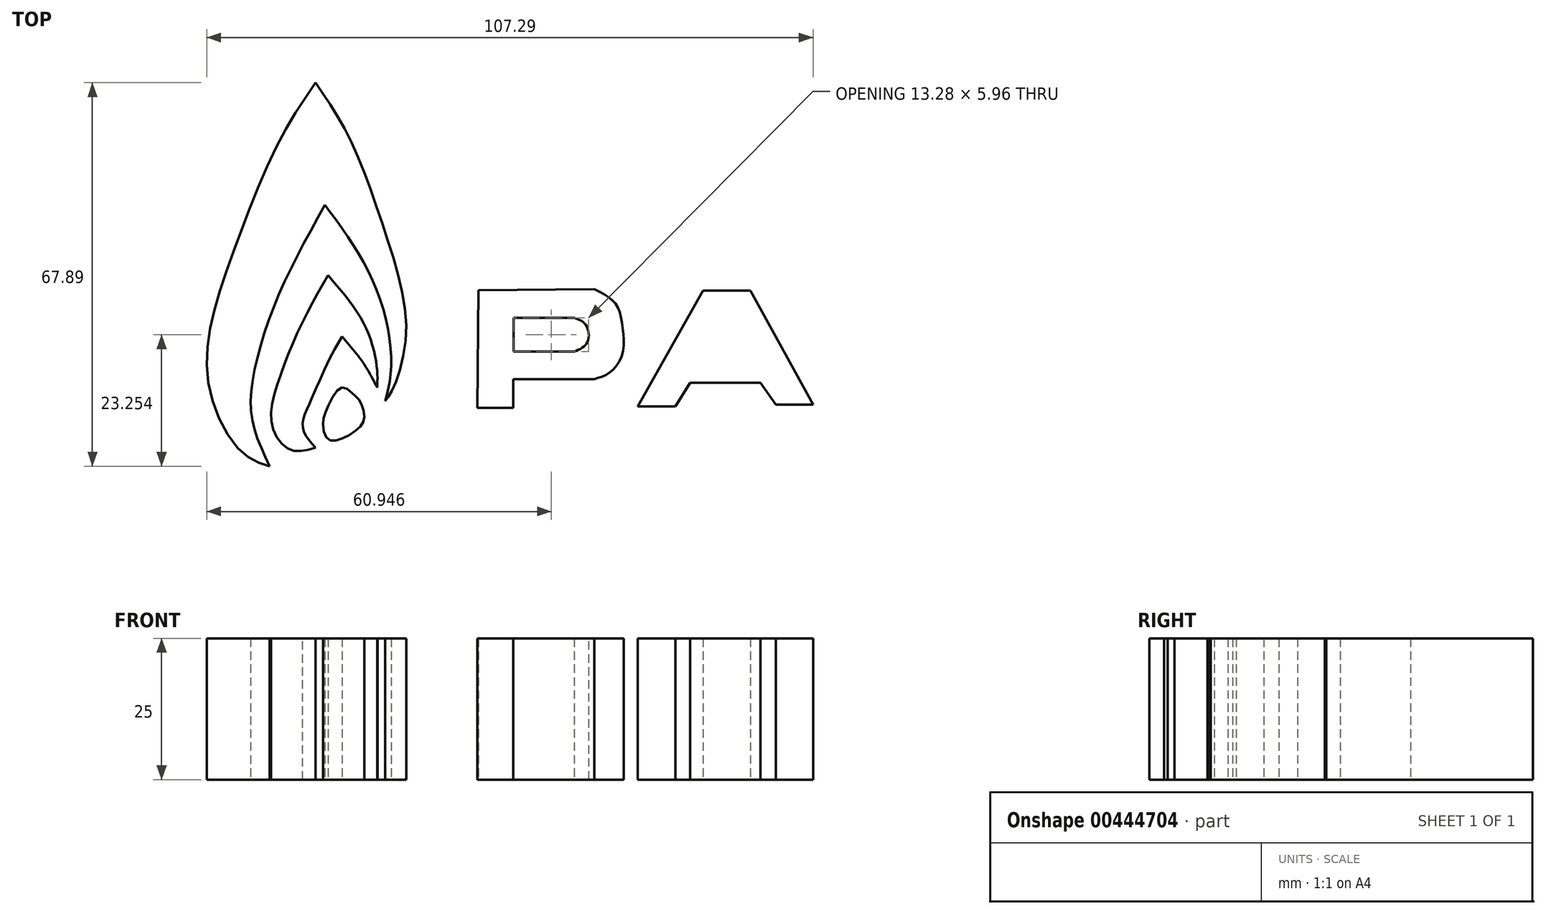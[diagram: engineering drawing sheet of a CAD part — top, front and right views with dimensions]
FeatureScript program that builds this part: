
annotation { "Feature Type Name" : "Feature", "Feature Type Description" : "" }
export const myFeature = defineFeature(function(context is Context, id is Id, definition is map)
    precondition{}
    {
        {
            var Q0;
            Q0=qCreatedBy(makeId("Top.planeOp"),FACE);
            var sketch = newSketch(context, id + "F0", { "sketchPlane" : qUnion([Q0])});
            skFitSpline(sketch, "E0", {"points": [v(-54.3, 49.44) * mm, v(-61.15, 38.22) * mm, v(-68.44, 20.5) * mm, v(-72.93, 5.9) * mm, v(-72.7, -6.22) * mm, v(-67.2, -16.09) * mm, v(-62.38, -18.45) * mm], "startDerivative": vector(-40.51, -59.93) * mm, "endDerivative": vector(44.37, -13.1) * mm});
            skFitSpline(sketch, "E1", {"points": [v(-62.38, -18.45) * mm, v(-65.4, -10.6) * mm, v(-65.19, -1.95) * mm, v(-60.8, 11.85) * mm, v(-52.62, 27.78) * mm], "startDerivative": vector(-17.84, 37.29) * mm, "endDerivative": vector(29.02, 52.05) * mm});
            skFitSpline(sketch, "E2", {"points": [v(-52.62, 27.78) * mm, v(-46.45, 18.8) * mm, v(-41.96, 8.15) * mm, v(-40.95, -1.61) * mm, v(-41.96, -6.89) * mm], "startDerivative": vector(23.8, -31.92) * mm, "endDerivative": vector(-6.8, -25.4) * mm});
            skFitSpline(sketch, "E3", {"points": [v(-41.96, -6.89) * mm, v(-40.72, -5) * mm, v(-38.25, 5.47) * mm, v(-41.96, 22.95) * mm, v(-48.32, 39.75) * mm, v(-54.3, 49.44) * mm], "startDerivative": vector(12.94, 16) * mm, "endDerivative": vector(-30.39, 43.69) * mm});
            skFitSpline(sketch, "E4", {"points": [v(-54.3, -15.17) * mm, v(-58.7, -15.57) * mm, v(-61.95, -11.32) * mm, v(-61.06, -4.1) * mm, v(-57.01, 6.16) * mm, v(-52.07, 15.35) * mm], "startDerivative": vector(-29.62, -8.98) * mm, "endDerivative": vector(21.55, 37.6) * mm});
            skFitSpline(sketch, "E5", {"points": [v(-52.07, 15.35) * mm, v(-45.46, 6.26) * mm, v(-43.38, -1.44) * mm, v(-43.38, -4.5) * mm], "startDerivative": vector(18, -20.75) * mm, "endDerivative": vector(-0.74, -12.27) * mm});
            skFitSpline(sketch, "E6", {"points": [v(-43.38, -4.5) * mm, v(-45.95, 0) * mm, v(-49.6, 4.48) * mm], "startDerivative": vector(-4.83, 9.4) * mm, "endDerivative": vector(-7.59, 8.6) * mm});
            skFitSpline(sketch, "E7", {"points": [v(-49.6, 4.48) * mm, v(-52.07, 0) * mm, v(-55.14, -6.89) * mm, v(-56.52, -11.62) * mm, v(-54.3, -15.17) * mm], "startDerivative": vector(-10.04, -17) * mm, "endDerivative": vector(13.81, -15.48) * mm});
            skFitSpline(sketch, "E8", {"points": [v(-49.6, -4.5) * mm, v(-52.07, -7.86) * mm, v(-52.96, -11.02) * mm, v(-52.07, -13.7) * mm, v(-49.6, -13.6) * mm, v(-46.45, -11.52) * mm, v(-45.65, -9.64) * mm, v(-46.45, -6.89) * mm, v(-47.63, -5.69) * mm, v(-49.6, -4.5) * mm]});
            skFitSpline(sketch, "E9", {"points": [v(-25.44, 12.72) * mm, v(-25.63, -8.14) * mm], "startDerivative": vector(-0.19, -20.86) * mm, "endDerivative": vector(-0.19, -20.86) * mm});
            skFitSpline(sketch, "E10", {"points": [v(-25.63, -8.14) * mm, v(-19.3, -8.14) * mm], "startDerivative": vector(6.33, 0) * mm, "endDerivative": vector(6.33, 0) * mm});
            skFitSpline(sketch, "E11", {"points": [v(-19.3, -8.14) * mm, v(-19.3, -3.02) * mm], "startDerivative": vector(0, 5.12) * mm, "endDerivative": vector(0, 5.12) * mm});
            skFitSpline(sketch, "E12", {"points": [v(-19.3, -3.02) * mm, v(-4.95, -3.02) * mm], "startDerivative": vector(14.34, 0) * mm, "endDerivative": vector(14.34, 0) * mm});
            skFitSpline(sketch, "E13", {"points": [v(-4.95, -3.02) * mm, v(-2.25, -1.9) * mm, v(0, 1.36) * mm, v(0, 6.67) * mm, v(-1.32, 10.49) * mm, v(-4.95, 12.9) * mm], "startDerivative": vector(16.44, 4.6) * mm, "endDerivative": vector(-20.28, 10.04) * mm});
            skFitSpline(sketch, "E14", {"points": [v(-25.44, 12.72) * mm, v(-4.95, 12.9) * mm], "startDerivative": vector(20.5, 0.19) * mm, "endDerivative": vector(20.5, 0.19) * mm});
            skLineSegment(sketch, "E15", {"start": v(-19.2, 7.32) * mm, "end": v(-19.2, 1.82) * mm});
            skLineSegment(sketch, "E16", {"start": v(-19.2, 1.82) * mm, "end": v(-8.5, 1.82) * mm});
            skFitSpline(sketch, "E17", {"points": [v(-8.5, 1.82) * mm, v(-6.16, 3.5) * mm, v(-6.44, 6.57) * mm, v(-8.5, 7.78) * mm], "startDerivative": vector(8.47, 3.6) * mm, "endDerivative": vector(-7.6, 2.47) * mm});
            skFitSpline(sketch, "E18", {"points": [v(-8.5, 7.78) * mm, v(-19.2, 7.78) * mm], "startDerivative": vector(-10.71, 0) * mm, "endDerivative": vector(-10.71, 0) * mm});
            skFitSpline(sketch, "E19", {"points": [v(-19.2, 7.78) * mm, v(-19.2, 7.32) * mm], "startDerivative": vector(0, -0.47) * mm, "endDerivative": vector(0, -0.47) * mm});
            skLineSegment(sketch, "E20", {"start": v(2.78, -7.86) * mm, "end": v(9.4, -7.86) * mm});
            skFitSpline(sketch, "E21", {"points": [v(9.4, -7.86) * mm, v(12, -3.67) * mm], "startDerivative": vector(2.6, 4.2) * mm, "endDerivative": vector(2.6, 4.2) * mm});
            skFitSpline(sketch, "E22", {"points": [v(12, -3.67) * mm, v(24.48, -3.67) * mm], "startDerivative": vector(12.48, 0) * mm, "endDerivative": vector(12.48, 0) * mm});
            skFitSpline(sketch, "E23", {"points": [v(24.48, -3.67) * mm, v(27.18, -7.58) * mm], "startDerivative": vector(2.7, -3.91) * mm, "endDerivative": vector(2.7, -3.91) * mm});
            skFitSpline(sketch, "E24", {"points": [v(27.18, -7.58) * mm, v(33.8, -7.58) * mm], "startDerivative": vector(6.61, 0) * mm, "endDerivative": vector(6.61, 0) * mm});
            skFitSpline(sketch, "E25", {"points": [v(33.89, -7.77) * mm, v(22.7, 12.63) * mm], "startDerivative": vector(-11.18, 20.4) * mm, "endDerivative": vector(-11.18, 20.4) * mm});
            skFitSpline(sketch, "E26", {"points": [v(22.7, 12.63) * mm, v(14.33, 12.63) * mm], "startDerivative": vector(-8.38, 0) * mm, "endDerivative": vector(-8.38, 0) * mm});
            skFitSpline(sketch, "E27", {"points": [v(14.33, 12.63) * mm, v(2.78, -7.86) * mm], "startDerivative": vector(-11.55, -20.5) * mm, "endDerivative": vector(-11.55, -20.5) * mm});
            skFitSpline(sketch, "E28", {"points": [v(17.77, 7.7) * mm, v(14.33, 0) * mm], "startDerivative": vector(-3.45, -7.7) * mm, "endDerivative": vector(-3.45, -7.7) * mm});
            skFitSpline(sketch, "E29", {"points": [v(14.33, 0) * mm, v(22.7, 0) * mm], "startDerivative": vector(8.38, 0) * mm, "endDerivative": vector(8.38, 0) * mm});
            skFitSpline(sketch, "E30", {"points": [v(22.34, 0.05) * mm, v(17.77, 7.7) * mm], "startDerivative": vector(-4.56, 7.64) * mm, "endDerivative": vector(-4.56, 7.64) * mm});
            skFitSpline(sketch, "E31", {"points": [v(39.85, 12.63) * mm, v(39.57, -7.86) * mm], "startDerivative": vector(-0.28, -20.5) * mm, "endDerivative": vector(-0.28, -20.5) * mm});
            skFitSpline(sketch, "E32", {"points": [v(39.57, -7.86) * mm, v(46.18, -7.86) * mm], "startDerivative": vector(6.61, 0) * mm, "endDerivative": vector(6.61, 0) * mm});
            skFitSpline(sketch, "E33", {"points": [v(46.18, -7.86) * mm, v(46.18, -2.93) * mm], "startDerivative": vector(0, 4.94) * mm, "endDerivative": vector(0, 4.94) * mm});
            skFitSpline(sketch, "E34", {"points": [v(46.18, -2.93) * mm, v(57.08, -2.93) * mm], "startDerivative": vector(10.9, 0) * mm, "endDerivative": vector(10.9, 0) * mm});
            skFitSpline(sketch, "E35", {"points": [v(57.08, -2.93) * mm, v(58.48, -2.93) * mm, v(58.85, -5.35) * mm, v(58.75, -7.86) * mm], "startDerivative": vector(6, 1.54) * mm, "endDerivative": vector(-0.29, -6.4) * mm});
            skFitSpline(sketch, "E36", {"points": [v(58.75, -7.86) * mm, v(65.09, -7.86) * mm], "startDerivative": vector(6.33, 0) * mm, "endDerivative": vector(6.33, 0) * mm});
            skFitSpline(sketch, "E37", {"points": [v(65.09, -7.68) * mm, v(65.27, -2.93) * mm], "startDerivative": vector(0.19, 4.75) * mm, "endDerivative": vector(0.19, 4.75) * mm});
            skFitSpline(sketch, "E38", {"points": [v(65.27, -2.93) * mm, v(65.27, -1.53) * mm, v(63.6, 0) * mm, v(62.39, 0) * mm], "startDerivative": vector(1.01, 4.36) * mm, "endDerivative": vector(-3.89, -0.84) * mm});
            skFitSpline(sketch, "E39", {"points": [v(62.76, 0.08) * mm, v(65.27, 2.29) * mm, v(65.27, 8.53) * mm, v(62.76, 12.44) * mm], "startDerivative": vector(10.48, 5.64) * mm, "endDerivative": vector(-8.8, 10.04) * mm});
            skFitSpline(sketch, "E40", {"points": [v(62.76, 12.44) * mm, v(39.85, 12.63) * mm], "startDerivative": vector(-22.92, 0.19) * mm, "endDerivative": vector(-22.92, 0.19) * mm});
            skFitSpline(sketch, "E41", {"points": [v(46.18, 7.5) * mm, v(46.18, 2) * mm], "startDerivative": vector(0, -5.5) * mm, "endDerivative": vector(0, -5.5) * mm});
            skFitSpline(sketch, "E42", {"points": [v(46.37, 2.2) * mm, v(58.79, 2.38) * mm], "startDerivative": vector(12.42, 0.19) * mm, "endDerivative": vector(12.42, 0.19) * mm});
            skFitSpline(sketch, "E43", {"points": [v(59.13, 2.66) * mm, v(59.5, 5.55) * mm, v(58.79, 7.7) * mm], "startDerivative": vector(1.3, 5.66) * mm, "endDerivative": vector(-2.04, 4.38) * mm});
            skFitSpline(sketch, "E44", {"points": [v(58.66, 7.88) * mm, v(46.18, 7.5) * mm], "startDerivative": vector(-12.48, -0.37) * mm, "endDerivative": vector(-12.48, -0.37) * mm});
            skFitSpline(sketch, "E45", {"points": [v(73.28, 8.9) * mm, v(73.28, -2.93) * mm], "startDerivative": vector(0, -11.83) * mm, "endDerivative": vector(0, -11.83) * mm});
            skFitSpline(sketch, "E46", {"points": [v(73.28, -2.93) * mm, v(74.5, -5.72) * mm, v(77.48, -7.86) * mm], "startDerivative": vector(1.79, -6.28) * mm, "endDerivative": vector(6.52, -3.63) * mm});
            skFitSpline(sketch, "E47", {"points": [v(77.94, -8.14) * mm, v(97.5, -7.86) * mm], "startDerivative": vector(19.56, 0.28) * mm, "endDerivative": vector(19.56, 0.28) * mm});
            skFitSpline(sketch, "E48", {"points": [v(97.5, -7.86) * mm, v(99.92, -7.08) * mm, v(101.41, -4.51) * mm], "startDerivative": vector(5.56, 0.82) * mm, "endDerivative": vector(2.3, 5.82) * mm});
            skFitSpline(sketch, "E49", {"points": [v(101.41, -4.51) * mm, v(101.41, 8.9) * mm], "startDerivative": vector(0, 13.41) * mm, "endDerivative": vector(0, 13.41) * mm});
            skFitSpline(sketch, "E50", {"points": [v(101.13, 9.46) * mm, v(100.2, 10.76) * mm, v(97.5, 12.44) * mm], "startDerivative": vector(-1.75, 3.2) * mm, "endDerivative": vector(-5.31, 2.79) * mm});
            skFitSpline(sketch, "E51", {"points": [v(97.5, 13) * mm, v(78.13, 12.44) * mm], "startDerivative": vector(-19.37, -0.56) * mm, "endDerivative": vector(-19.37, -0.56) * mm});
            skFitSpline(sketch, "E52", {"points": [v(77.48, 12.53) * mm, v(74.68, 11.5) * mm, v(73.28, 8.9) * mm], "startDerivative": vector(-6.28, -1.25) * mm, "endDerivative": vector(-2.1, -6.02) * mm});
            skFitSpline(sketch, "E53", {"points": [v(92.75, 7.5) * mm, v(82.32, 7.5) * mm], "startDerivative": vector(-10.43, 0) * mm, "endDerivative": vector(-10.43, 0) * mm});
            skFitSpline(sketch, "E54", {"points": [v(82.23, 7.5) * mm, v(80.83, 7.04) * mm, v(80, 5.27) * mm], "startDerivative": vector(-3.34, -0.47) * mm, "endDerivative": vector(-1.18, -3.92) * mm});
            skFitSpline(sketch, "E55", {"points": [v(80.08, 4.25) * mm, v(80.18, -1.16) * mm], "startDerivative": vector(0.1, -5.4) * mm, "endDerivative": vector(0.1, -5.4) * mm});
            skFitSpline(sketch, "E56", {"points": [v(80.18, -1.16) * mm, v(80.83, -1.72) * mm, v(82.97, -2.46) * mm], "startDerivative": vector(1.38, -1.52) * mm, "endDerivative": vector(4, -1.12) * mm});
            skFitSpline(sketch, "E57", {"points": [v(83.06, -2.65) * mm, v(93.3, -2.93) * mm], "startDerivative": vector(10.25, -0.28) * mm, "endDerivative": vector(10.25, -0.28) * mm});
            skFitSpline(sketch, "E58", {"points": [v(93.12, -2.83) * mm, v(93.87, -1.8) * mm, v(95.08, 0) * mm], "startDerivative": vector(1.63, 2.19) * mm, "endDerivative": vector(2.25, 3.42) * mm});
            skFitSpline(sketch, "E59", {"points": [v(95.27, 0.52) * mm, v(95.08, 5.83) * mm], "startDerivative": vector(-0.19, 5.3) * mm, "endDerivative": vector(-0.19, 5.3) * mm});
            skFitSpline(sketch, "E60", {"points": [v(94.9, 6.01) * mm, v(94.24, 6.67) * mm, v(92.75, 7.5) * mm], "startDerivative": vector(-1.32, 1.56) * mm, "endDerivative": vector(-2.89, 1.43) * mm});
            skFitSpline(sketch, "E61", {"points": [v(106.81, 12.63) * mm, v(114.08, 12.44) * mm], "startDerivative": vector(7.26, -0.19) * mm, "endDerivative": vector(7.26, -0.19) * mm});
            skFitSpline(sketch, "E62", {"points": [v(114.17, 12.53) * mm, v(121.25, 4.52) * mm], "startDerivative": vector(7.08, -8.01) * mm, "endDerivative": vector(7.08, -8.01) * mm});
            skFitSpline(sketch, "E63", {"points": [v(121.34, 4.52) * mm, v(127.68, 12.63) * mm], "startDerivative": vector(6.33, 8.1) * mm, "endDerivative": vector(6.33, 8.1) * mm});
            skFitSpline(sketch, "E64", {"points": [v(127.77, 12.63) * mm, v(134.76, 12.53) * mm], "startDerivative": vector(6.99, -0.1) * mm, "endDerivative": vector(6.99, -0.1) * mm});
            skFitSpline(sketch, "E65", {"points": [v(135.13, 12.07) * mm, v(124.51, 0) * mm], "startDerivative": vector(-10.62, -12.07) * mm, "endDerivative": vector(-10.62, -12.07) * mm});
            skFitSpline(sketch, "E66", {"points": [v(124.7, -0.41) * mm, v(124.14, -7.58) * mm], "startDerivative": vector(-0.56, -7.17) * mm, "endDerivative": vector(-0.56, -7.17) * mm});
            skFitSpline(sketch, "E67", {"points": [v(124.42, -8.52) * mm, v(118.36, -7.86) * mm], "startDerivative": vector(-6.05, 0.65) * mm, "endDerivative": vector(-6.05, 0.65) * mm});
            skFitSpline(sketch, "E68", {"points": [v(118.08, -7.96) * mm, v(118.18, -0.6) * mm], "startDerivative": vector(0.1, 7.36) * mm, "endDerivative": vector(0.1, 7.36) * mm});
            skFitSpline(sketch, "E69", {"points": [v(118, -0.6) * mm, v(106.81, 12.63) * mm], "startDerivative": vector(-11.18, 13.23) * mm, "endDerivative": vector(-11.18, 13.23) * mm});
            skSolve(sketch);
        }
        {
            var Q0;
            Q0 = qSketchRegion(id + "F0", true);
            extrude(context, id + "F1", {"entities" : qUnion([Q0]), "depth" : 25 * mm});
        }
    });
